# Revit family: Finestra sporgente vetrata
name_source: partatom
category: Finestre
revit_build: Autodesk Revit 2018 (Build: 20170223_1515(x64)
units: mm (PartAtom-declared; Revit-internal decimal feet)

## family parameters
Condiviso = No
Host = Muro
Punto di calcolo locali = No
Sempre verticale = Sì
Taglio con vuoti quando caricato = No

## types (5) — shared parameters
Chiusura muro = Per host
Coefficiente di scambio termico (U) = 3.6886 W/(m²·K)
Costruzione analitica = Vetrata singola Pilkington 1/8 in
ID tipo di costruzione = GSP4R
Indice di riscaldamento alla radiazione solare = 0.78
Produttore = Revit
Resistenza termica (R) = 0.2711 (m²·K)/W
Trasmittanza luminosa = 0.9

## per-type parameters (varying)
| type | Altezza | Altezza soglia | Davanzale | Larghezza | Sporgenza davanzale | Telaio/montante | Vetro |
| 100 x 100 cm | 1000 mm  [stored 3.28084 ft] | 800 mm  [stored 2.62467 ft] | Rame | 1000 mm  [stored 3.28084 ft] | 68 mm | Acciaio, carbonio | Vetro Colorato |
| 120 x 120 cm | 2500 mm | 100 mm  [stored 0.328084 ft] | Acciaio inossidabile | 1200 mm | 68 mm | Acciaio inossidabile | Vetro |
| 80 x 80 cm | 800 mm  [stored 2.62467 ft] | 900 mm  [stored 2.95276 ft] | Rame | 800 mm  [stored 2.62467 ft] | 50 mm  [stored 0.164042 ft] | Acciaio, carbonio | Vetro Colorato |
| 120 x 270 | 2700 mm  [stored 8.85827 ft] | 100 mm  [stored 0.328084 ft] | Acciaio inossidabile | 1200 mm | 68 mm | Acciaio inossidabile | Vetro |
| 120 x 250 | 2500 mm | 100 mm  [stored 0.328084 ft] | Acciaio inossidabile | 1200 mm | 68 mm | Acciaio inossidabile | Vetro |

note: [stored X ft] marks values corroborated as IEEE doubles in the binary element streams (Revit-internal decimal feet)
